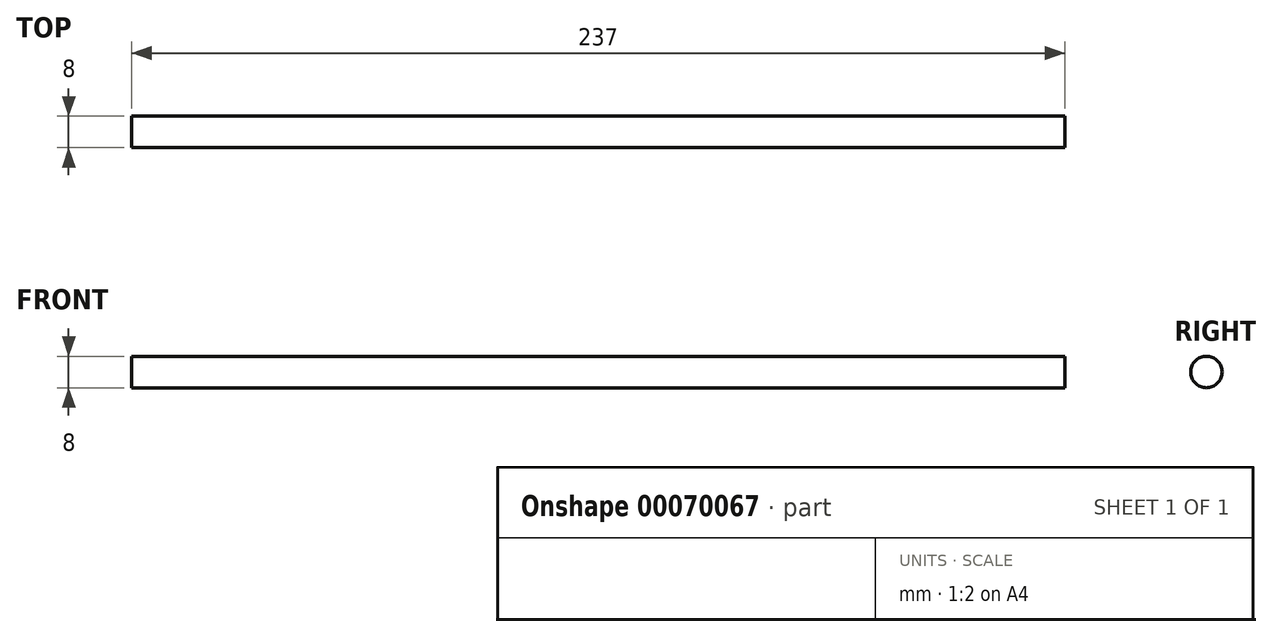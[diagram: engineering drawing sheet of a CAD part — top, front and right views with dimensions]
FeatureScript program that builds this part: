
annotation { "Feature Type Name" : "Feature", "Feature Type Description" : "" }
export const myFeature = defineFeature(function(context is Context, id is Id, definition is map)
    precondition{}
    {
        {
            var Q0;
            Q0=qCreatedBy(makeId("Top.planeOp"),FACE);
            var sketch = newSketch(context, id + "F0", { "sketchPlane" : qUnion([Q0])});
            skLineSegment(sketch, "E0.bottom", {"start": v(-118.5, 0) * mm, "end": v(118.5, 0) * mm});
            skLineSegment(sketch, "E0.top", {"start": v(-118.5, 4) * mm, "end": v(118.5, 4) * mm});
            skLineSegment(sketch, "E0.left", {"start": v(-118.5, 0) * mm, "end": v(-118.5, 4) * mm});
            skLineSegment(sketch, "E0.right", {"start": v(118.5, 0) * mm, "end": v(118.5, 4) * mm});
            skSolve(sketch);
        }
        {
            var Q0;
            Q0 = qSketchRegion(id + "F0", true);
            var Q1;
            Q1=sQuery(id+"F0.wireOp",EDGE,"E0.bottom");
            revolve(context, id + "F1", {"entities" : qUnion([Q0]), "axis" : qUnion([Q1]), "revolveType" : RevolveType.FULL});
        }
    });
